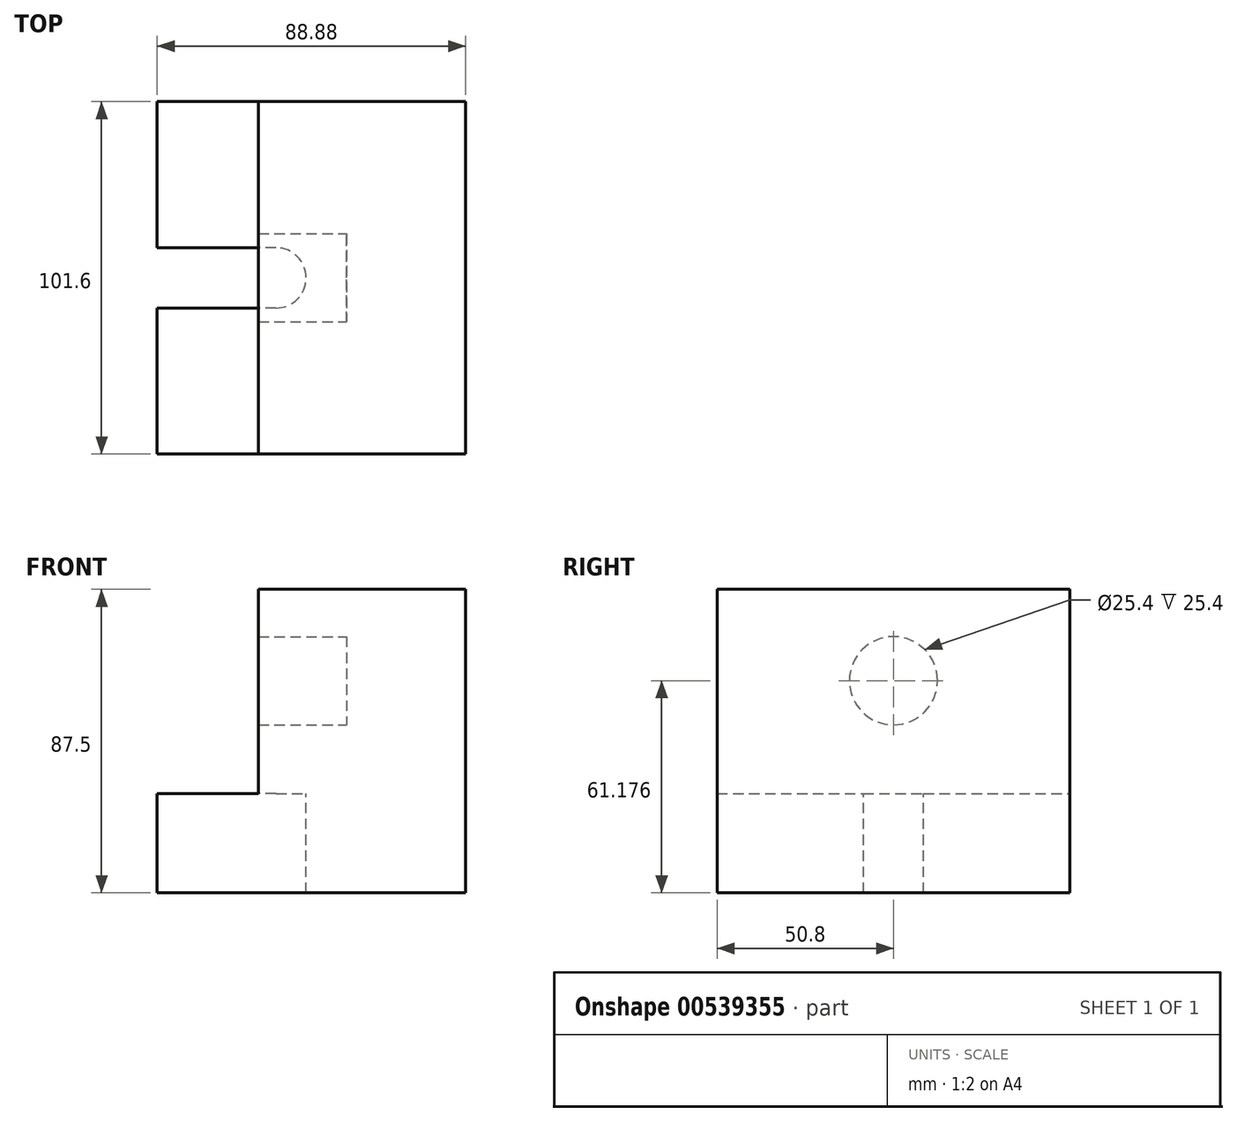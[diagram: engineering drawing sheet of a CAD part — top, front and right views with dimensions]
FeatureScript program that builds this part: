
annotation { "Feature Type Name" : "Feature", "Feature Type Description" : "" }
export const myFeature = defineFeature(function(context is Context, id is Id, definition is map)
    precondition{}
    {
        {
            var Q0;
            Q0=qCreatedBy(makeId("Front.planeOp"),FACE);
            var sketch = newSketch(context, id + "F0", { "sketchPlane" : qUnion([Q0])});
            skLineSegment(sketch, "E0.bottom", {"start": v(17.15, 43.75) * mm, "end": v(-17.15, 43.75) * mm});
            skLineSegment(sketch, "E0.top", {"start": v(17.15, -43.75) * mm, "end": v(-17.15, -43.75) * mm});
            skLineSegment(sketch, "E0.left", {"start": v(17.15, 43.75) * mm, "end": v(17.15, -43.75) * mm});
            skLineSegment(sketch, "E0.right", {"start": v(-17.15, 43.75) * mm, "end": v(-17.15, -15.17) * mm});
            skPoint(sketch, "E0.middle", {"position": v(0, 0) * mm});
            skLineSegment(sketch, "E1.bottom", {"start": v(17.15, -43.75) * mm, "end": v(-71.73, -43.75) * mm});
            skLineSegment(sketch, "E1.top", {"start": v(-17.15, -15.17) * mm, "end": v(-71.73, -15.17) * mm});
            skLineSegment(sketch, "E1.left", {"start": v(17.15, -43.75) * mm, "end": v(17.15, -15.17) * mm});
            skLineSegment(sketch, "E1.right", {"start": v(-71.73, -43.75) * mm, "end": v(-71.73, -15.17) * mm});
            skSolve(sketch);
        }
        {
            var Q0;
            Q0 = qSketchRegion(id + "F0", true);
            extrude(context, id + "F1", {"entities" : qUnion([Q0]), "endBound" : BoundingType.SYMMETRIC, "depth" : 101.6 * mm, "offsetDistance" : 25.4 * mm});
        }
        {
            var Q0;
            Q0=makeQuery(id+"F1.opExtrude","SWEPT_FACE",FACE,{"disambiguationData":[OSD([sQuery(id+"F0.wireOp",EDGE,"E1.top")])]});
            var sketch = newSketch(context, id + "F2", { "sketchPlane" : qUnion([Q0])});
            skCircle(sketch, "E2", {"center": v(-37.47, 0) * mm, "radius": 8.68 * mm});
            skLineSegment(sketch, "E3", {"start": v(-37.47, 8.68) * mm, "end": v(-71.73, 8.68) * mm});
            skLineSegment(sketch, "E4", {"start": v(-37.47, -8.68) * mm, "end": v(-71.73, -8.68) * mm});
            skLineSegment(sketch, "E5", {"start": v(-71.73, -8.68) * mm, "end": v(-71.73, 8.68) * mm});
            skSolve(sketch);
        }
        {
            var Q0;
            {var subQ0=sQuery(id+"F2.wireOp",EDGE,"E3");Q0=makeQuery(id+"F2.imprint","IMPRINT",FACE,{"disambiguationData":[TD([[makeQuery(id+"F2.imprint","IMPRINT",EDGE,{"derivedFrom":subQ0}),1.0]])]});}
            var Q1;
            {var subQ0=sQuery(id+"F2.wireOp",EDGE,"E2");var subQ1=makeQuery(id+"F2.imprint","INTERSECT",VERTEX,{"derivedFrom":[subQ0,sQuery(id+"F2.wireOp",EDGE,"E3")]});Q1=makeQuery(id+"F2.imprint","IMPRINT",FACE,{"disambiguationData":[TD([[makeQuery(id+"F2.imprint","IMPRINT",EDGE,{"disambiguationData":[TD([[subQ1,-1.0]])],"derivedFrom":subQ0}),1.0]])]});}
            extrude(context, id + "F3", {"entities" : qUnion([Q0, Q1]), "operationType" : NewBodyOperationType.REMOVE, "endBound" : BoundingType.UP_TO_NEXT, "oppositeDirection" : true, "depth" : 25.4 * mm, "offsetDistance" : 25.4 * mm});
        }
        {
            var Q0;
            Q0=makeQuery(id+"F1.opExtrude","SWEPT_FACE",FACE,{"disambiguationData":[OSD([sQuery(id+"F0.wireOp",EDGE,"E0.right")])]});
            var sketch = newSketch(context, id + "F4", { "sketchPlane" : qUnion([Q0])});
            skCircle(sketch, "E6", {"center": v(0, 17.43) * mm, "radius": 12.7 * mm});
            skSolve(sketch);
        }
        {
            var Q0;
            Q0=makeQuery(id+"F4.imprint","IMPRINT",FACE,{"disambiguationData":[TD([[makeQuery(id+"F4.imprint","IMPRINT",EDGE,{"derivedFrom":sQuery(id+"F4.wireOp",EDGE,"E6")}),-1.0]])]});
            extrude(context, id + "F5", {"entities" : qUnion([Q0]), "operationType" : NewBodyOperationType.ADD, "depth" : 25.4 * mm, "offsetDistance" : 25.4 * mm});
        }
    });
